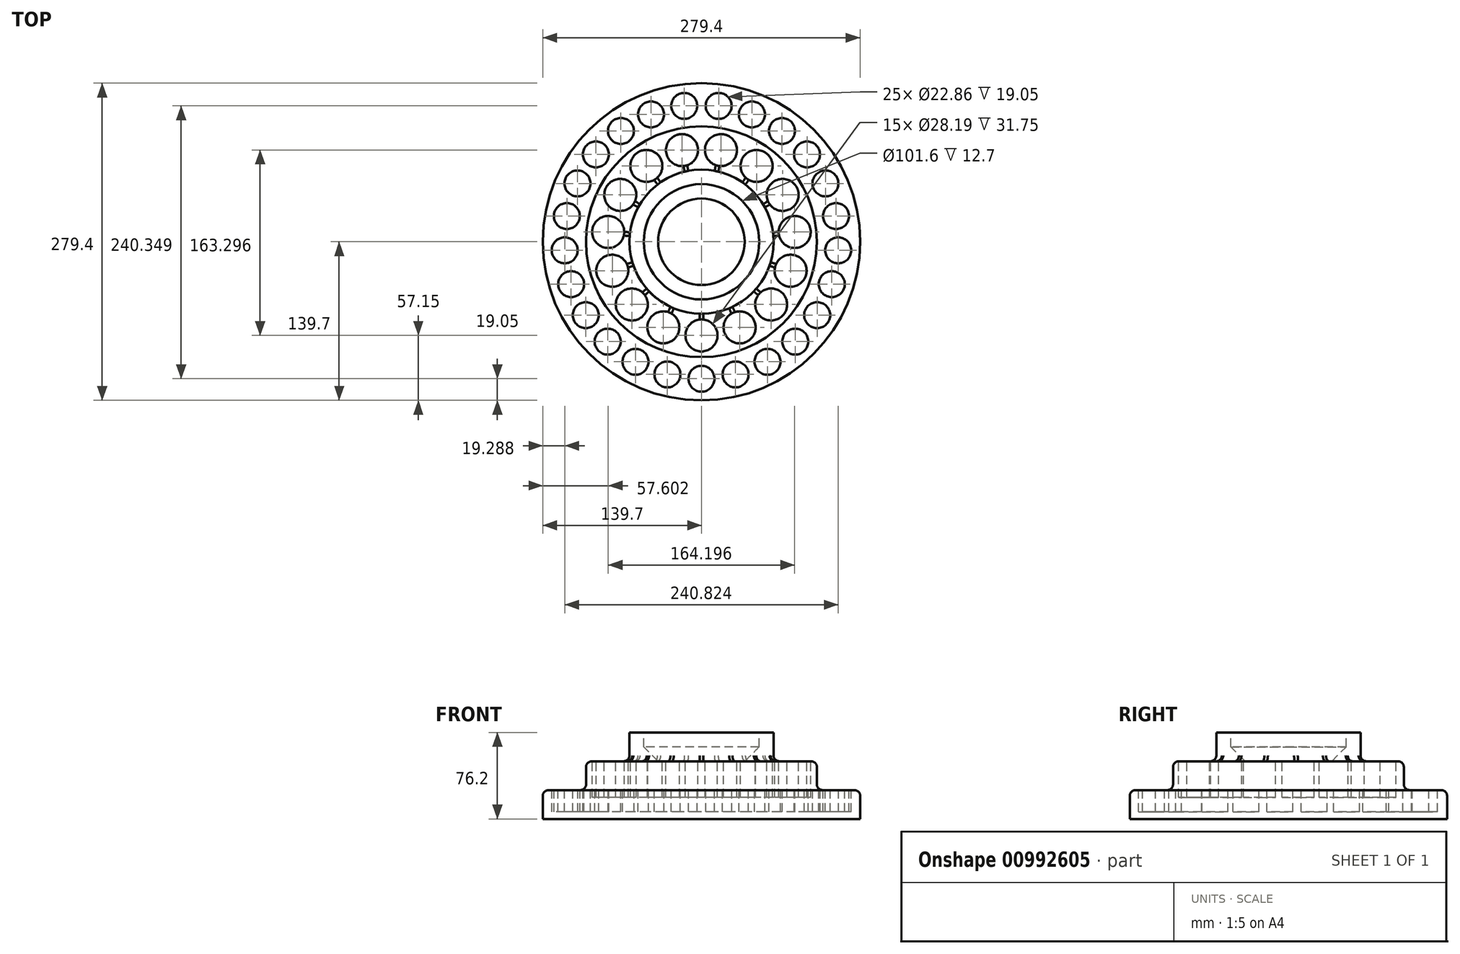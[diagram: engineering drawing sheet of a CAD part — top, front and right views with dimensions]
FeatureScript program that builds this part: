
annotation { "Feature Type Name" : "Feature", "Feature Type Description" : "" }
export const myFeature = defineFeature(function(context is Context, id is Id, definition is map)
    precondition{}
    {
        {
            var Q0;
            Q0=qCreatedBy(makeId("Right.planeOp"),FACE);
            var sketch = newSketch(context, id + "F0", { "sketchPlane" : qUnion([Q0])});
            skLineSegment(sketch, "E0", {"start": v(0, 0) * mm, "end": v(0, -76.2) * mm});
            skLineSegment(sketch, "E1", {"start": v(0, -76.2) * mm, "end": v(-139.7, -76.2) * mm});
            skLineSegment(sketch, "E2", {"start": v(-139.7, -76.2) * mm, "end": v(-139.7, -50.8) * mm});
            skLineSegment(sketch, "E3", {"start": v(-139.7, -50.8) * mm, "end": v(-101.6, -50.8) * mm});
            skLineSegment(sketch, "E4", {"start": v(-101.6, -50.8) * mm, "end": v(-101.6, -25.4) * mm});
            skLineSegment(sketch, "E5", {"start": v(-101.6, -25.4) * mm, "end": v(-63.5, -25.4) * mm});
            skLineSegment(sketch, "E6", {"start": v(-63.5, -25.4) * mm, "end": v(-63.5, 0) * mm});
            skLineSegment(sketch, "E7", {"start": v(-63.5, 0) * mm, "end": v(0, 0) * mm});
            skSolve(sketch);
        }
        {
            var Q0;
            Q0 = qSketchRegion(id + "F0", true);
            var Q1;
            Q1=sQuery(id+"F0.wireOp",EDGE,"E0");
            revolve(context, id + "F1", {"surfaceOperationType" : NewSurfaceOperationType.NEW, "entities" : qUnion([Q0]), "axis" : qUnion([Q1]), "revolveType" : RevolveType.FULL});
        }
        {
            var Q0;
            Q0=makeQuery(id+"F1.opRevolve","SWEPT_FACE",FACE,{"disambiguationData":[OSD([sQuery(id+"F0.wireOp",EDGE,"E3")])]});
            var sketch = newSketch(context, id + "F2", { "sketchPlane" : qUnion([Q0])});
            skLineSegment(sketch, "E8", {"start": v(0, -139.7) * mm, "end": v(0, -101.6) * mm, "construction": true});
            skLineSegment(sketch, "E9", {"start": v(0, -101.6) * mm, "end": v(0, -120.65) * mm, "construction": true});
            skCircle(sketch, "E10", {"center": v(0, -120.65) * mm, "radius": 11.43 * mm});
            skCircle(sketch, "E11.1.0", {"center": v(30, -116.86) * mm, "radius": 11.43 * mm});
            skCircle(sketch, "E11.2.0", {"center": v(58.12, -105.73) * mm, "radius": 11.43 * mm});
            skCircle(sketch, "E11.3.0", {"center": v(82.6, -87.95) * mm, "radius": 11.43 * mm});
            skCircle(sketch, "E11.4.0", {"center": v(101.87, -64.65) * mm, "radius": 11.43 * mm});
            skCircle(sketch, "E11.5.0", {"center": v(114.74, -37.28) * mm, "radius": 11.43 * mm});
            skCircle(sketch, "E11.6.0", {"center": v(120.41, -7.58) * mm, "radius": 11.43 * mm});
            skCircle(sketch, "E11.7.0", {"center": v(118.51, 22.6) * mm, "radius": 11.43 * mm});
            skCircle(sketch, "E11.8.0", {"center": v(109.17, 51.37) * mm, "radius": 11.43 * mm});
            skCircle(sketch, "E11.9.0", {"center": v(92.96, 76.9) * mm, "radius": 11.43 * mm});
            skCircle(sketch, "E11.10.0", {"center": v(70.92, 97.6) * mm, "radius": 11.43 * mm});
            skCircle(sketch, "E11.11.0", {"center": v(44.41, 112.18) * mm, "radius": 11.43 * mm});
            skCircle(sketch, "E11.12.0", {"center": v(15.12, 119.7) * mm, "radius": 11.43 * mm});
            skCircle(sketch, "E11.13.0", {"center": v(-15.12, 119.7) * mm, "radius": 11.43 * mm});
            skCircle(sketch, "E11.14.0", {"center": v(-44.41, 112.18) * mm, "radius": 11.43 * mm});
            skCircle(sketch, "E11.15.0", {"center": v(-70.92, 97.6) * mm, "radius": 11.43 * mm});
            skCircle(sketch, "E11.16.0", {"center": v(-92.96, 76.9) * mm, "radius": 11.43 * mm});
            skCircle(sketch, "E11.17.0", {"center": v(-109.17, 51.37) * mm, "radius": 11.43 * mm});
            skCircle(sketch, "E11.18.0", {"center": v(-118.51, 22.6) * mm, "radius": 11.43 * mm});
            skCircle(sketch, "E11.19.0", {"center": v(-120.41, -7.58) * mm, "radius": 11.43 * mm});
            skCircle(sketch, "E11.20.0", {"center": v(-114.74, -37.28) * mm, "radius": 11.43 * mm});
            skCircle(sketch, "E11.21.0", {"center": v(-101.87, -64.65) * mm, "radius": 11.43 * mm});
            skCircle(sketch, "E11.22.0", {"center": v(-82.6, -87.95) * mm, "radius": 11.43 * mm});
            skCircle(sketch, "E11.23.0", {"center": v(-58.12, -105.73) * mm, "radius": 11.43 * mm});
            skCircle(sketch, "E11.24.0", {"center": v(-30, -116.86) * mm, "radius": 11.43 * mm});
            skPoint(sketch, "E11.center", {"position": v(0, 0) * mm});
            skSolve(sketch);
        }
        {
            var Q0;
            Q0 = qSketchRegion(id + "F2", true);
            extrude(context, id + "F3", {"entities" : qUnion([Q0]), "operationType" : NewBodyOperationType.REMOVE, "oppositeDirection" : true, "depth" : 19.05 * mm, "offsetDistance" : 25.4 * mm});
        }
        {
            var Q0;
            Q0=makeQuery(id+"F1.opRevolve","SWEPT_FACE",FACE,{"disambiguationData":[OSD([sQuery(id+"F0.wireOp",EDGE,"E5")])]});
            var sketch = newSketch(context, id + "F4", { "sketchPlane" : qUnion([Q0])});
            skLineSegment(sketch, "E12", {"start": v(0, -101.6) * mm, "end": v(0, -63.5) * mm, "construction": true});
            skLineSegment(sketch, "E13", {"start": v(0, -63.5) * mm, "end": v(0, -82.55) * mm, "construction": true});
            skCircle(sketch, "E14", {"center": v(0, -82.55) * mm, "radius": 14.1 * mm});
            skCircle(sketch, "E15.1.0", {"center": v(33.58, -75.41) * mm, "radius": 14.1 * mm});
            skCircle(sketch, "E15.2.0", {"center": v(61.35, -55.24) * mm, "radius": 14.1 * mm});
            skCircle(sketch, "E15.3.0", {"center": v(78.5, -25.5) * mm, "radius": 14.1 * mm});
            skCircle(sketch, "E15.4.0", {"center": v(82.1, 8.63) * mm, "radius": 14.1 * mm});
            skCircle(sketch, "E15.5.0", {"center": v(71.5, 41.27) * mm, "radius": 14.1 * mm});
            skCircle(sketch, "E15.6.0", {"center": v(48.52, 66.78) * mm, "radius": 14.1 * mm});
            skCircle(sketch, "E15.7.0", {"center": v(17.16, 80.75) * mm, "radius": 14.1 * mm});
            skCircle(sketch, "E15.8.0", {"center": v(-17.16, 80.75) * mm, "radius": 14.1 * mm});
            skCircle(sketch, "E15.9.0", {"center": v(-48.52, 66.78) * mm, "radius": 14.1 * mm});
            skCircle(sketch, "E15.10.0", {"center": v(-71.5, 41.28) * mm, "radius": 14.1 * mm});
            skCircle(sketch, "E15.11.0", {"center": v(-82.1, 8.63) * mm, "radius": 14.1 * mm});
            skCircle(sketch, "E15.12.0", {"center": v(-78.5, -25.5) * mm, "radius": 14.1 * mm});
            skCircle(sketch, "E15.13.0", {"center": v(-61.35, -55.24) * mm, "radius": 14.1 * mm});
            skCircle(sketch, "E15.14.0", {"center": v(-33.58, -75.41) * mm, "radius": 14.1 * mm});
            skPoint(sketch, "E15.center", {"position": v(0, 0) * mm});
            skSolve(sketch);
        }
        {
            var Q0;
            Q0 = qSketchRegion(id + "F4", true);
            extrude(context, id + "F5", {"entities" : qUnion([Q0]), "operationType" : NewBodyOperationType.REMOVE, "oppositeDirection" : true, "depth" : 31.75 * mm, "offsetDistance" : 25.4 * mm});
        }
        {
            var Q0;
            Q0=makeQuery(id+"F1.opRevolve","SWEPT_FACE",FACE,{"disambiguationData":[OSD([sQuery(id+"F0.wireOp",EDGE,"E7")])]});
            var sketch = newSketch(context, id + "F6", { "sketchPlane" : qUnion([Q0])});
            skCircle(sketch, "E16", {"center": v(0, 0) * mm, "radius": 50.8 * mm});
            skSolve(sketch);
        }
        {
            var Q0;
            Q0 = qSketchRegion(id + "F6", true);
            extrude(context, id + "F7", {"entities" : qUnion([Q0]), "operationType" : NewBodyOperationType.REMOVE, "oppositeDirection" : true, "depth" : 25.4 * mm, "offsetDistance" : 25.4 * mm});
        }
        {
            var Q0;
            Q0=makeQuery(id+"F7.boolean.opBoolean","COPY",EDGE,{"derivedFrom":makeQuery(id+"F7.opExtrude","CAP_EDGE",EDGE,{"disambiguationData":[OSD([sQuery(id+"F6.wireOp",EDGE,"E16")])],"isStart":false})});
            var Q1;
            Q1=makeQuery(id+"F7.boolean.opBoolean","COPY",EDGE,{"derivedFrom":makeQuery(id+"F7.opExtrude","CAP_EDGE",EDGE,{"disambiguationData":[OSD([sQuery(id+"F6.wireOp",EDGE,"E16")])],"isStart":true})});
            chamfer(context, id + "F8", {"entities" : qUnion([Q0, Q1]), "width" : 12.7 * mm, "tangentPropagation" : true});
        }
        {
            var Q0;
            Q0=makeQuery(id+"F1.opRevolve","SWEPT_EDGE",EDGE,{"disambiguationData":[OSD([sQuery(id+"F0.wireOp",EDGE,"E2"),sQuery(id+"F0.wireOp",EDGE,"E3")])]});
            var Q1;
            Q1=makeQuery(id+"F1.opRevolve","SWEPT_EDGE",EDGE,{"disambiguationData":[OSD([sQuery(id+"F0.wireOp",EDGE,"E3"),sQuery(id+"F0.wireOp",EDGE,"E4")])]});
            var Q2;
            Q2=makeQuery(id+"F1.opRevolve","SWEPT_EDGE",EDGE,{"disambiguationData":[OSD([sQuery(id+"F0.wireOp",EDGE,"E4"),sQuery(id+"F0.wireOp",EDGE,"E5")])]});
            var Q3;
            Q3=makeQuery(id+"F8.opChamfer","BLEND_EDGE",EDGE,{"blendedFrom":[makeQuery(id+"F7.boolean.opBoolean","COPY",EDGE,{"derivedFrom":makeQuery(id+"F7.opExtrude","CAP_EDGE",EDGE,{"disambiguationData":[OSD([sQuery(id+"F6.wireOp",EDGE,"E16")])],"isStart":true})}),makeQuery(id+"F1.opRevolve","SWEPT_FACE",FACE,{"disambiguationData":[OSD([sQuery(id+"F0.wireOp",EDGE,"E6")])]})],"blendedInto":[makeQuery(id+"F1.opRevolve","SWEPT_FACE",FACE,{"disambiguationData":[OSD([sQuery(id+"F0.wireOp",EDGE,"E6")])]})]});
            var Q4;
            Q4=makeQuery(id+"F1.opRevolve","SWEPT_EDGE",EDGE,{"disambiguationData":[OSD([sQuery(id+"F0.wireOp",EDGE,"E5"),sQuery(id+"F0.wireOp",EDGE,"E6")])]});
            fillet(context, id + "F9", {"entities" : qUnion([Q0, Q1, Q2, Q3, Q4]), "radius" : 5.08 * mm, "tangentPropagation" : true, "allowEdgeOverflow" : false});
        }
    });
